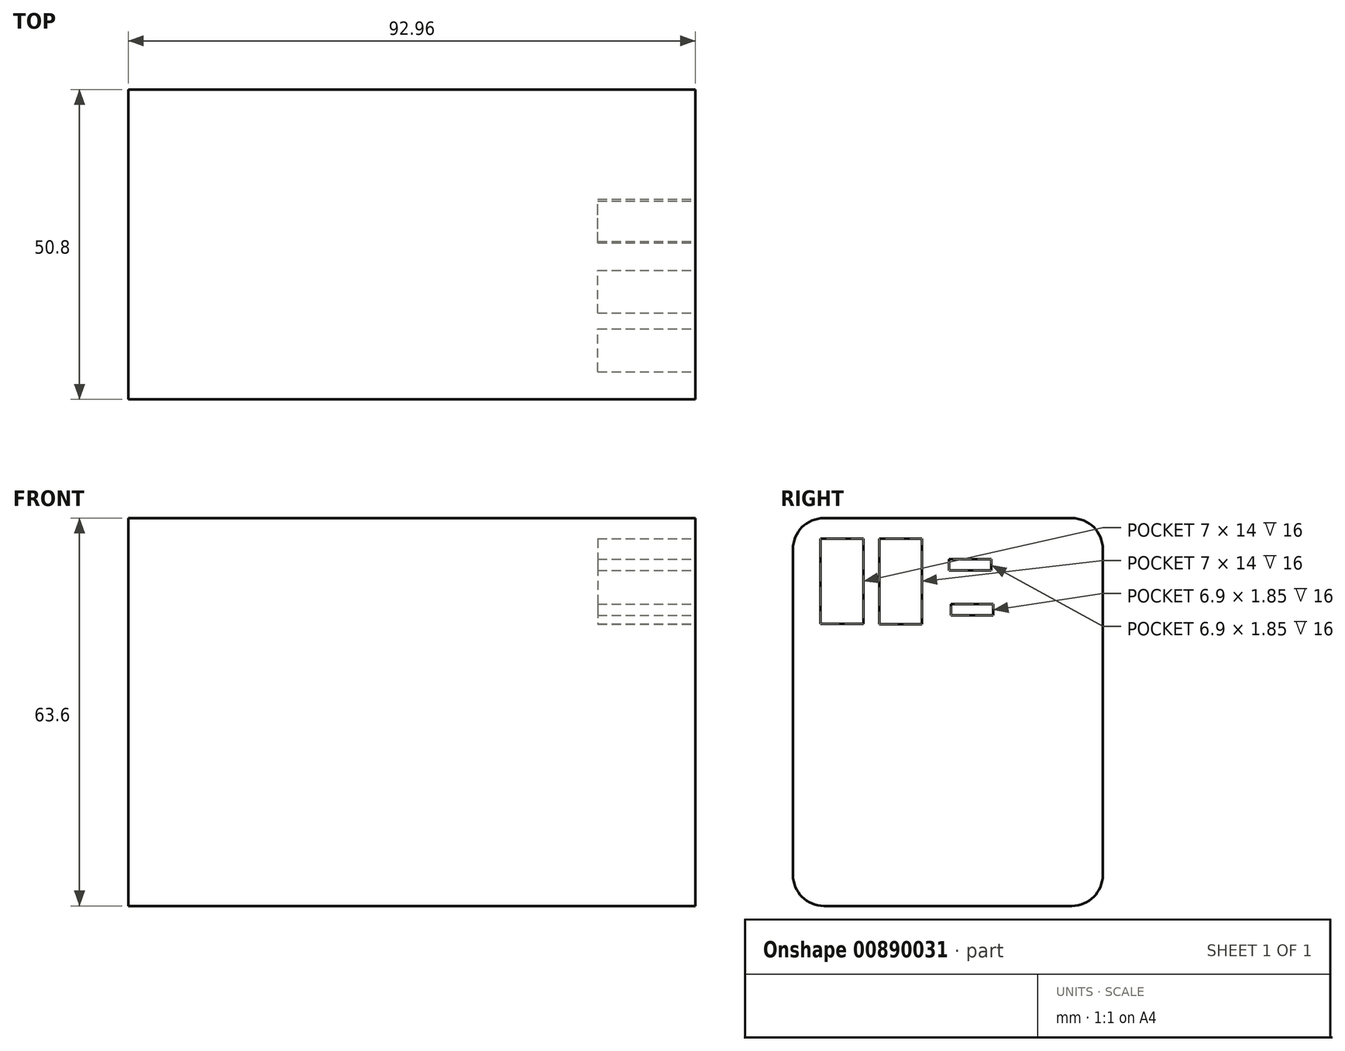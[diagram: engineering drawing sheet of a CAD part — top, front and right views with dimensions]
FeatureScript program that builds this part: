
annotation { "Feature Type Name" : "Feature", "Feature Type Description" : "" }
export const myFeature = defineFeature(function(context is Context, id is Id, definition is map)
    precondition{}
    {
        {
            var Q0;
            Q0=qCreatedBy(makeId("Front.planeOp"),FACE);
            var sketch = newSketch(context, id + "F0", { "sketchPlane" : qUnion([Q0])});
            skLineSegment(sketch, "E0.bottom", {"start": v(-46.48, 31.8) * mm, "end": v(46.48, 31.8) * mm});
            skLineSegment(sketch, "E0.top", {"start": v(-46.48, -31.8) * mm, "end": v(46.48, -31.8) * mm});
            skLineSegment(sketch, "E0.left", {"start": v(-46.48, 31.8) * mm, "end": v(-46.48, -31.8) * mm});
            skLineSegment(sketch, "E0.right", {"start": v(46.48, 31.8) * mm, "end": v(46.48, -31.8) * mm});
            skPoint(sketch, "E0.middle", {"position": v(0, 0) * mm});
            skSolve(sketch);
        }
        {
            var Q0;
            Q0=makeQuery(id+"F0.imprint","IMPRINT",FACE,{"disambiguationData":[TD([[makeQuery(id+"F0.imprint","IMPRINT",EDGE,{"derivedFrom":sQuery(id+"F0.wireOp",EDGE,"E0.bottom")}),-1.0]])]});
            extrude(context, id + "F1", {"entities" : qUnion([Q0]), "depth" : 50.8 * mm, "offsetDistance" : 25.4 * mm});
        }
        {
            var Q0;
            Q0=makeQuery(id+"F1.opExtrude","SWEPT_FACE",FACE,{"disambiguationData":[OSD([sQuery(id+"F0.wireOp",EDGE,"E0.right")])]});
            var sketch = newSketch(context, id + "F2", { "sketchPlane" : qUnion([Q0])});
            skSolve(sketch);
        }
        {
            var Q0;
            {var subQ0=sQuery(id+"F0.wireOp",EDGE,"E0.right");Q0=makeQuery(id+"F2.imprint","IMPRINT",FACE,{"disambiguationData":[TD([[makeQuery(id+"F2.imprint","IMPRINT",EDGE,{"derivedFrom":makeQuery(id+"F1.opExtrude","CAP_EDGE",EDGE,{"disambiguationData":[OSD([subQ0])],"isStart":true})}),-1.0]])]});}
            var sketch = newSketch(context, id + "F3", { "sketchPlane" : qUnion([Q0])});
            skSolve(sketch);
        }
        {
            var Q0;
            Q0=makeQuery(id+"F1.opExtrude","CAP_EDGE",EDGE,{"disambiguationData":[OSD([sQuery(id+"F0.wireOp",EDGE,"E0.bottom")])],"isStart":false});
            fillet(context, id + "F4", {"entities" : qUnion([Q0]), "radius" : 5.08 * mm, "tangentPropagation" : true, "allowEdgeOverflow" : false});
        }
        {
            var Q0;
            Q0=makeQuery(id+"F1.opExtrude","CAP_EDGE",EDGE,{"disambiguationData":[OSD([sQuery(id+"F0.wireOp",EDGE,"E0.bottom")])],"isStart":true});
            fillet(context, id + "F5", {"entities" : qUnion([Q0]), "radius" : 5.08 * mm, "tangentPropagation" : true, "allowEdgeOverflow" : false});
        }
        {
            var Q0;
            Q0=makeQuery(id+"F1.opExtrude","CAP_EDGE",EDGE,{"disambiguationData":[OSD([sQuery(id+"F0.wireOp",EDGE,"E0.top")])],"isStart":false});
            var Q1;
            Q1=makeQuery(id+"F1.opExtrude","CAP_EDGE",EDGE,{"disambiguationData":[OSD([sQuery(id+"F0.wireOp",EDGE,"E0.top")])],"isStart":true});
            fillet(context, id + "F6", {"entities" : qUnion([Q0, Q1]), "radius" : 5.08 * mm, "tangentPropagation" : true, "allowEdgeOverflow" : false});
        }
        {
            var Q0;
            {var subQ0=sQuery(id+"F0.wireOp",EDGE,"E0.right");Q0=makeQuery(id+"F3.imprint","IMPRINT",FACE,{"disambiguationData":[TD([[makeQuery(id+"F3.imprint","IMPRINT",EDGE,{"derivedFrom":makeQuery(id+"F2.imprint","IMPRINT",EDGE,{"derivedFrom":makeQuery(id+"F1.opExtrude","CAP_EDGE",EDGE,{"disambiguationData":[OSD([subQ0])],"isStart":true})})}),-1.0]])]});}
            var sketch = newSketch(context, id + "F7", { "sketchPlane" : qUnion([Q0])});
            skLineSegment(sketch, "E1.bottom", {"start": v(-46.27, 28.44) * mm, "end": v(-39.27, 28.44) * mm});
            skLineSegment(sketch, "E1.top", {"start": v(-46.27, 14.44) * mm, "end": v(-39.27, 14.44) * mm});
            skLineSegment(sketch, "E1.left", {"start": v(-46.27, 28.44) * mm, "end": v(-46.27, 14.44) * mm});
            skLineSegment(sketch, "E1.right", {"start": v(-39.27, 28.44) * mm, "end": v(-39.27, 14.44) * mm});
            skSolve(sketch);
        }
        {
            var Q0;
            Q0 = qSketchRegion(id + "F7", true);
            extrude(context, id + "F8", {"entities" : qUnion([Q0]), "operationType" : NewBodyOperationType.REMOVE, "oppositeDirection" : true, "depth" : 16 * mm, "offsetDistance" : 25.4 * mm});
        }
        {
            var Q0;
            {var subQ0=sQuery(id+"F0.wireOp",EDGE,"E0.right");Q0=makeQuery(id+"F3.imprint","IMPRINT",FACE,{"disambiguationData":[TD([[makeQuery(id+"F3.imprint","IMPRINT",EDGE,{"derivedFrom":makeQuery(id+"F2.imprint","IMPRINT",EDGE,{"derivedFrom":makeQuery(id+"F1.opExtrude","CAP_EDGE",EDGE,{"disambiguationData":[OSD([subQ0])],"isStart":true})})}),-1.0]])]});}
            var sketch = newSketch(context, id + "F9", { "sketchPlane" : qUnion([Q0])});
            skLineSegment(sketch, "E2.bottom", {"start": v(-36.67, 28.43) * mm, "end": v(-29.67, 28.43) * mm});
            skLineSegment(sketch, "E2.top", {"start": v(-36.67, 14.43) * mm, "end": v(-29.67, 14.43) * mm});
            skLineSegment(sketch, "E2.left", {"start": v(-36.67, 28.43) * mm, "end": v(-36.67, 14.43) * mm});
            skLineSegment(sketch, "E2.right", {"start": v(-29.67, 28.43) * mm, "end": v(-29.67, 14.43) * mm});
            skSolve(sketch);
        }
        {
            var Q0;
            Q0 = qSketchRegion(id + "F9", true);
            extrude(context, id + "F10", {"entities" : qUnion([Q0]), "operationType" : NewBodyOperationType.REMOVE, "oppositeDirection" : true, "depth" : 16 * mm, "offsetDistance" : 25.4 * mm});
        }
        {
            var Q0;
            {var subQ0=sQuery(id+"F0.wireOp",EDGE,"E0.right");Q0=makeQuery(id+"F3.imprint","IMPRINT",FACE,{"disambiguationData":[TD([[makeQuery(id+"F3.imprint","IMPRINT",EDGE,{"derivedFrom":makeQuery(id+"F2.imprint","IMPRINT",EDGE,{"derivedFrom":makeQuery(id+"F1.opExtrude","CAP_EDGE",EDGE,{"disambiguationData":[OSD([subQ0])],"isStart":true})})}),-1.0]])]});}
            var sketch = newSketch(context, id + "F11", { "sketchPlane" : qUnion([Q0])});
            skLineSegment(sketch, "E3.bottom", {"start": v(-25.18, 25.05) * mm, "end": v(-18.28, 25.05) * mm});
            skLineSegment(sketch, "E3.top", {"start": v(-25.18, 23.2) * mm, "end": v(-18.28, 23.2) * mm});
            skLineSegment(sketch, "E3.left", {"start": v(-25.18, 25.05) * mm, "end": v(-25.18, 23.2) * mm});
            skLineSegment(sketch, "E3.right", {"start": v(-18.28, 25.05) * mm, "end": v(-18.28, 23.2) * mm});
            skLineSegment(sketch, "E4.bottom", {"start": v(-24.9, 17.69) * mm, "end": v(-18, 17.69) * mm});
            skLineSegment(sketch, "E4.top", {"start": v(-24.9, 15.84) * mm, "end": v(-18, 15.84) * mm});
            skLineSegment(sketch, "E4.left", {"start": v(-24.9, 17.69) * mm, "end": v(-24.9, 15.84) * mm});
            skLineSegment(sketch, "E4.right", {"start": v(-18, 17.69) * mm, "end": v(-18, 15.84) * mm});
            skSolve(sketch);
        }
        {
            var Q0;
            Q0 = qSketchRegion(id + "F11", true);
            extrude(context, id + "F12", {"entities" : qUnion([Q0]), "operationType" : NewBodyOperationType.REMOVE, "oppositeDirection" : true, "depth" : 16 * mm, "offsetDistance" : 25.4 * mm});
        }
    });
